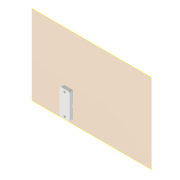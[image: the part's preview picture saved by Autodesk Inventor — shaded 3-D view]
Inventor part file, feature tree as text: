
AUTODESK INVENTOR PART (.ipt)
format: ipt  version: 2022 (Build 260153000, 153)  size: 105,984 bytes
history: native  units: mm
features: reference x4, other x4, extrude x2, sketch x2, plane x1, fillet x1
ambient origin geometry x8: Origin, YZ Plane, XZ Plane, XY Plane, X Axis, Y Axis, Z Axis, Center Point
bodies: Volumenkörper1 (feature_tree)
feature tree (14):
  plane  "Arbeitsebene1"
  extrude  "Extrusion1"  Depth=3.0mm
  fillet  "Rundung1"  Radius=3.0mm
  extrude  "Extrusion2"  Depth=4.0mm TaperAngle=0.0deg
  sketch  "Skizze1"  dims[d0=24.953762mm d1=3.0mm d2=3.0mm]
  reference  "Referenz1"
  reference  "Referenz2"
  reference  "Referenz3"
  sketch  "Skizze2"  dims[d3=12.0mm d4=4.0mm d5=0.0mm d6=2.0mm d7=11.0mm d8=4.0mm d9=0.0mm]
  reference  "Referenz4"
  other  "<userpath>\Documents\GitHub\Guinardia\INVENTOR\Assembly_Guinardia_V1.iam"
  other  "Assembly_Guinardia_V1.iam"
  other  "10_Wellplate_base_v1:1"
  other  "20_SMAConnector_fiber:1"
